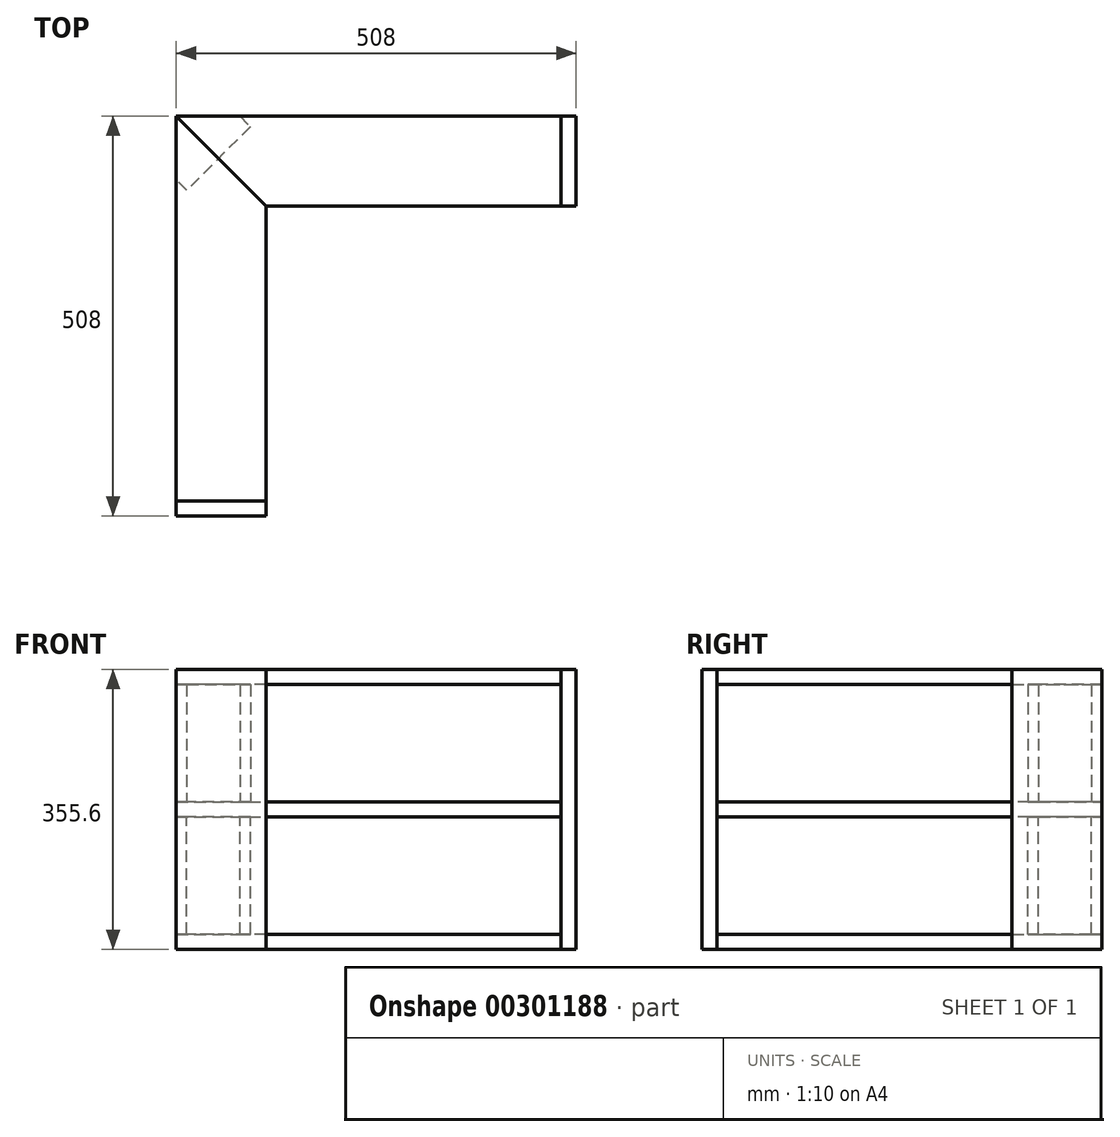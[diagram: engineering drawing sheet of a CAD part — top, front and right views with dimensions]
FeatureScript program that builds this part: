
annotation { "Feature Type Name" : "Feature", "Feature Type Description" : "" }
export const myFeature = defineFeature(function(context is Context, id is Id, definition is map)
    precondition{}
    {
        {
            var Q0;
            Q0=qCreatedBy(makeId("Top.planeOp"),FACE);
            var sketch = newSketch(context, id + "F0", { "sketchPlane" : qUnion([Q0])});
            skLineSegment(sketch, "E0", {"start": v(0, -374.65) * mm, "end": v(-114.3, -374.65) * mm});
            skLineSegment(sketch, "E1", {"start": v(-114.3, -374.65) * mm, "end": v(-114.3, 114.3) * mm});
            skLineSegment(sketch, "E2", {"start": v(-114.3, 114.3) * mm, "end": v(393.7, 114.3) * mm});
            skLineSegment(sketch, "E3", {"start": v(393.7, 114.3) * mm, "end": v(393.7, 0) * mm});
            skLineSegment(sketch, "E4", {"start": v(393.7, 0) * mm, "end": v(0, 0) * mm});
            skLineSegment(sketch, "E5", {"start": v(0, 0) * mm, "end": v(0, -374.65) * mm});
            skLineSegment(sketch, "E6", {"start": v(0, 0) * mm, "end": v(-114.3, 114.3) * mm});
            skSolve(sketch);
        }
        {
            var Q0;
            Q0=makeQuery(id+"F0.imprint","IMPRINT",FACE,{"disambiguationData":[TD([[makeQuery(id+"F0.imprint","IMPRINT",EDGE,{"derivedFrom":sQuery(id+"F0.wireOp",EDGE,"E0")}),-1.0]])]});
            extrude(context, id + "F1", {"entities" : qUnion([Q0]), "depth" : 19.05 * mm});
        }
        {
            var Q0;
            Q0=makeQuery(id+"F1.opExtrude","CAP_FACE",FACE,{"disambiguationData":[OSD([sQuery(id+"F0.wireOp",EDGE,"E0"),sQuery(id+"F0.wireOp",EDGE,"E1"),sQuery(id+"F0.wireOp",EDGE,"E5"),sQuery(id+"F0.wireOp",EDGE,"E6")])],"isStart":true});
            var sketch = newSketch(context, id + "F2", { "sketchPlane" : qUnion([Q0])});
            skLineSegment(sketch, "E7", {"start": v(-114.3, -114.3) * mm, "end": v(374.65, -114.3) * mm});
            skLineSegment(sketch, "E8", {"start": v(374.65, -114.3) * mm, "end": v(374.65, 0) * mm});
            skLineSegment(sketch, "E9", {"start": v(374.65, 0) * mm, "end": v(0, 0) * mm});
            skLineSegment(sketch, "E10", {"start": v(-114.3, -114.3) * mm, "end": v(0, 0) * mm});
            skSolve(sketch);
        }
        {
            var Q0;
            Q0=makeQuery(id+"F2.imprint","IMPRINT",FACE,{"disambiguationData":[TD([[makeQuery(id+"F2.imprint","IMPRINT",EDGE,{"derivedFrom":sQuery(id+"F2.wireOp",EDGE,"E7")}),1.0]])]});
            extrude(context, id + "F3", {"entities" : qUnion([Q0]), "oppositeDirection" : true, "depth" : 19.05 * mm});
        }
        {
            var Q0;
            Q0=makeQuery(id+"F1.opExtrude","SWEPT_FACE",FACE,{"disambiguationData":[OSD([sQuery(id+"F0.wireOp",EDGE,"E0")])]});
            var sketch = newSketch(context, id + "F4", { "sketchPlane" : qUnion([Q0])});
            skLineSegment(sketch, "E11.bottom", {"start": v(-114.3, 0) * mm, "end": v(0, 0) * mm});
            skLineSegment(sketch, "E11.top", {"start": v(-114.3, 355.6) * mm, "end": v(0, 355.6) * mm});
            skLineSegment(sketch, "E11.left", {"start": v(-114.3, 0) * mm, "end": v(-114.3, 355.6) * mm});
            skLineSegment(sketch, "E11.right", {"start": v(0, 0) * mm, "end": v(0, 355.6) * mm});
            skSolve(sketch);
        }
        {
            var Q0;
            {var subQ0=sQuery(id+"F4.wireOp",EDGE,"E11.top");Q0=makeQuery(id+"F4.imprint","IMPRINT",FACE,{"disambiguationData":[TD([[makeQuery(id+"F4.imprint","IMPRINT",EDGE,{"derivedFrom":subQ0}),-1.0]])]});}
            var Q1;
            {var subQ0=sQuery(id+"F4.wireOp",EDGE,"E11.bottom");Q1=makeQuery(id+"F4.imprint","IMPRINT",FACE,{"disambiguationData":[TD([[makeQuery(id+"F4.imprint","IMPRINT",EDGE,{"derivedFrom":subQ0}),-1.0]])]});}
            extrude(context, id + "F5", {"entities" : qUnion([Q0, Q1]), "depth" : 19.05 * mm});
        }
        {
            var Q0;
            Q0=makeQuery(id+"F3.opExtrude","SWEPT_FACE",FACE,{"disambiguationData":[OSD([sQuery(id+"F2.wireOp",EDGE,"E8")])]});
            var sketch = newSketch(context, id + "F6", { "sketchPlane" : qUnion([Q0])});
            skLineSegment(sketch, "E12.bottom", {"start": v(0, 0) * mm, "end": v(114.3, 0) * mm});
            skLineSegment(sketch, "E12.top", {"start": v(0, 355.6) * mm, "end": v(114.3, 355.6) * mm});
            skLineSegment(sketch, "E12.left", {"start": v(0, 0) * mm, "end": v(0, 355.6) * mm});
            skLineSegment(sketch, "E12.right", {"start": v(114.3, 0) * mm, "end": v(114.3, 355.6) * mm});
            skSolve(sketch);
        }
        {
            var Q0;
            {var subQ0=sQuery(id+"F6.wireOp",EDGE,"E12.top");Q0=makeQuery(id+"F6.imprint","IMPRINT",FACE,{"disambiguationData":[TD([[makeQuery(id+"F6.imprint","IMPRINT",EDGE,{"derivedFrom":subQ0}),-1.0]])]});}
            var Q1;
            {var subQ0=sQuery(id+"F6.wireOp",EDGE,"E12.bottom");Q1=makeQuery(id+"F6.imprint","IMPRINT",FACE,{"disambiguationData":[TD([[makeQuery(id+"F6.imprint","IMPRINT",EDGE,{"derivedFrom":subQ0}),-1.0]])]});}
            extrude(context, id + "F7", {"entities" : qUnion([Q0, Q1]), "depth" : 19.05 * mm});
        }
        {
            var Q0;
            Q0=makeQuery(id+"F1.opExtrude","CAP_FACE",FACE,{"disambiguationData":[OSD([sQuery(id+"F0.wireOp",EDGE,"E0"),sQuery(id+"F0.wireOp",EDGE,"E1"),sQuery(id+"F0.wireOp",EDGE,"E5"),sQuery(id+"F0.wireOp",EDGE,"E6")])],"isStart":true});
            cPlane(context, id + "F8", {"entities" : qUnion([Q0]), "cplaneType" : CPlaneType.OFFSET, "offset" : 355.6 * mm, "oppositeDirection" : true, "width" : 152.4 * mm, "height" : 152.4 * mm});
        }
        {
            var Q0;
            Q0=qCreatedBy(id+"F8.planeOp",FACE);
            var sketch = newSketch(context, id + "F9", { "sketchPlane" : qUnion([Q0])});
            skLineSegment(sketch, "E13", {"start": v(-114.3, -114.3) * mm, "end": v(-114.3, 374.65) * mm});
            skLineSegment(sketch, "E14", {"start": v(-114.3, 374.65) * mm, "end": v(0, 374.65) * mm});
            skLineSegment(sketch, "E15", {"start": v(0, 374.65) * mm, "end": v(0, 0) * mm});
            skLineSegment(sketch, "E16", {"start": v(0, 0) * mm, "end": v(-114.3, -114.3) * mm});
            skSolve(sketch);
        }
        {
            var Q0;
            Q0 = qSketchRegion(id + "F9", true);
            extrude(context, id + "F10", {"entities" : qUnion([Q0]), "depth" : 19.05 * mm});
        }
        {
            var Q0;
            Q0=qCreatedBy(id+"F8.planeOp",FACE);
            var sketch = newSketch(context, id + "F11", { "sketchPlane" : qUnion([Q0])});
            skLineSegment(sketch, "E17", {"start": v(0, 0) * mm, "end": v(-114.3, -114.3) * mm});
            skLineSegment(sketch, "E18", {"start": v(-114.3, -114.3) * mm, "end": v(374.65, -114.3) * mm});
            skLineSegment(sketch, "E19", {"start": v(374.65, -114.3) * mm, "end": v(374.65, 0) * mm});
            skLineSegment(sketch, "E20", {"start": v(374.65, 0) * mm, "end": v(0, 0) * mm});
            skSolve(sketch);
        }
        {
            var Q0;
            Q0=makeQuery(id+"F11.imprint","IMPRINT",FACE,{"disambiguationData":[TD([[makeQuery(id+"F11.imprint","IMPRINT",EDGE,{"derivedFrom":sQuery(id+"F11.wireOp",EDGE,"E17")}),1.0]])]});
            extrude(context, id + "F12", {"entities" : qUnion([Q0]), "depth" : 19.05 * mm});
        }
        {
            var Q0;
            Q0=makeQuery(id+"F10.opExtrude","CAP_FACE",FACE,{"disambiguationData":[OSD([sQuery(id+"F9.wireOp",EDGE,"E13"),sQuery(id+"F9.wireOp",EDGE,"E14"),sQuery(id+"F9.wireOp",EDGE,"E15"),sQuery(id+"F9.wireOp",EDGE,"E16")])],"isStart":false});
            var Q1;
            Q1=makeQuery(id+"F1.opExtrude","CAP_FACE",FACE,{"disambiguationData":[OSD([sQuery(id+"F0.wireOp",EDGE,"E0"),sQuery(id+"F0.wireOp",EDGE,"E1"),sQuery(id+"F0.wireOp",EDGE,"E5"),sQuery(id+"F0.wireOp",EDGE,"E6")])],"isStart":false});
            cPlane(context, id + "F13", {"entities" : qUnion([Q0, Q1]), "cplaneType" : CPlaneType.MID_PLANE, "offset" : 25.4 * mm, "width" : 152.4 * mm, "height" : 152.4 * mm});
        }
        {
            var Q0;
            Q0=qCreatedBy(id+"F13.planeOp",FACE);
            var sketch = newSketch(context, id + "F14", { "sketchPlane" : qUnion([Q0])});
            skLineSegment(sketch, "E21", {"start": v(-114.3, 374.65) * mm, "end": v(0, 374.65) * mm});
            skLineSegment(sketch, "E22", {"start": v(0, 374.65) * mm, "end": v(0, 0) * mm});
            skLineSegment(sketch, "E23", {"start": v(0, 0) * mm, "end": v(-114.3, -114.3) * mm});
            skLineSegment(sketch, "E24", {"start": v(-114.3, -114.3) * mm, "end": v(-114.3, 374.65) * mm});
            skSolve(sketch);
        }
        {
            var Q0;
            Q0=makeQuery(id+"F14.imprint","IMPRINT",FACE,{"disambiguationData":[TD([[makeQuery(id+"F14.imprint","IMPRINT",EDGE,{"derivedFrom":sQuery(id+"F14.wireOp",EDGE,"E21")}),-1.0]])]});
            extrude(context, id + "F15", {"entities" : qUnion([Q0]), "endBound" : BoundingType.SYMMETRIC, "depth" : 19.05 * mm});
        }
        {
            var Q0;
            Q0=qCreatedBy(id+"F13.planeOp",FACE);
            var sketch = newSketch(context, id + "F16", { "sketchPlane" : qUnion([Q0])});
            skLineSegment(sketch, "E25", {"start": v(-114.3, -114.3) * mm, "end": v(0, 0) * mm});
            skLineSegment(sketch, "E26", {"start": v(0, 0) * mm, "end": v(374.65, 0) * mm});
            skLineSegment(sketch, "E27", {"start": v(374.65, 0) * mm, "end": v(374.65, -114.3) * mm});
            skLineSegment(sketch, "E28", {"start": v(374.65, -114.3) * mm, "end": v(-114.3, -114.3) * mm});
            skSolve(sketch);
        }
        {
            var Q0;
            Q0=makeQuery(id+"F16.imprint","IMPRINT",FACE,{"disambiguationData":[TD([[makeQuery(id+"F16.imprint","IMPRINT",EDGE,{"derivedFrom":sQuery(id+"F16.wireOp",EDGE,"E25")}),-1.0]])]});
            extrude(context, id + "F17", {"entities" : qUnion([Q0]), "endBound" : BoundingType.SYMMETRIC, "depth" : 19.05 * mm});
        }
        {
            var Q0;
            Q0=makeQuery(id+"F17.opExtrude","CAP_FACE",FACE,{"disambiguationData":[OSD([sQuery(id+"F16.wireOp",EDGE,"E25"),sQuery(id+"F16.wireOp",EDGE,"E26"),sQuery(id+"F16.wireOp",EDGE,"E27"),sQuery(id+"F16.wireOp",EDGE,"E28")])],"isStart":true});
            var sketch = newSketch(context, id + "F18", { "sketchPlane" : qUnion([Q0])});
            skLineSegment(sketch, "E29", {"start": v(-33.48, 114.3) * mm, "end": v(-20, 100.83) * mm});
            skLineSegment(sketch, "E30", {"start": v(-20, 100.83) * mm, "end": v(-100.83, 20) * mm});
            skLineSegment(sketch, "E31", {"start": v(-100.83, 20) * mm, "end": v(-114.3, 33.48) * mm});
            skLineSegment(sketch, "E32", {"start": v(-114.3, 33.48) * mm, "end": v(-33.48, 114.3) * mm});
            skSolve(sketch);
        }
        {
            var Q0;
            {var subQ0=sQuery(id+"F18.wireOp",EDGE,"E29");Q0=makeQuery(id+"F18.imprint","IMPRINT",FACE,{"disambiguationData":[TD([[makeQuery(id+"F18.imprint","IMPRINT",EDGE,{"derivedFrom":subQ0}),-1.0]])]});}
            var Q1;
            {var subQ0=sQuery(id+"F18.wireOp",EDGE,"E31");Q1=makeQuery(id+"F18.imprint","IMPRINT",FACE,{"disambiguationData":[TD([[makeQuery(id+"F18.imprint","IMPRINT",EDGE,{"derivedFrom":subQ0}),-1.0]])]});}
            var Q2;
            Q2=makeQuery(id+"F12.opExtrude","CAP_FACE",FACE,{"disambiguationData":[OSD([sQuery(id+"F11.wireOp",EDGE,"E17"),sQuery(id+"F11.wireOp",EDGE,"E18"),sQuery(id+"F11.wireOp",EDGE,"E19"),sQuery(id+"F11.wireOp",EDGE,"E20")])],"isStart":false});
            extrude(context, id + "F19", {"entities" : qUnion([Q0, Q1]), "endBound" : BoundingType.UP_TO_SURFACE, "endBoundEntityFace" : qUnion([Q2]), "depth" : 25.4 * mm});
        }
        {
            var Q0;
            Q0=makeQuery(id+"F17.opExtrude","CAP_FACE",FACE,{"disambiguationData":[OSD([sQuery(id+"F16.wireOp",EDGE,"E25"),sQuery(id+"F16.wireOp",EDGE,"E26"),sQuery(id+"F16.wireOp",EDGE,"E27"),sQuery(id+"F16.wireOp",EDGE,"E28")])],"isStart":false});
            var sketch = newSketch(context, id + "F20", { "sketchPlane" : qUnion([Q0])});
            skLineSegment(sketch, "E33", {"start": v(-33.48, -114.3) * mm, "end": v(-20, -100.83) * mm});
            skLineSegment(sketch, "E34", {"start": v(-20, -100.83) * mm, "end": v(-100.83, -20) * mm});
            skLineSegment(sketch, "E35", {"start": v(-100.83, -20) * mm, "end": v(-114.3, -33.48) * mm});
            skLineSegment(sketch, "E36", {"start": v(-114.3, -33.48) * mm, "end": v(-33.48, -114.3) * mm});
            skSolve(sketch);
        }
        {
            var Q0;
            {var subQ0=sQuery(id+"F20.wireOp",EDGE,"E35");Q0=makeQuery(id+"F20.imprint","IMPRINT",FACE,{"disambiguationData":[TD([[makeQuery(id+"F20.imprint","IMPRINT",EDGE,{"derivedFrom":subQ0}),1.0]])]});}
            var Q1;
            {var subQ0=sQuery(id+"F20.wireOp",EDGE,"E33");Q1=makeQuery(id+"F20.imprint","IMPRINT",FACE,{"disambiguationData":[TD([[makeQuery(id+"F20.imprint","IMPRINT",EDGE,{"derivedFrom":subQ0}),1.0]])]});}
            var Q2;
            Q2=makeQuery(id+"F3.opExtrude","CAP_FACE",FACE,{"disambiguationData":[OSD([sQuery(id+"F2.wireOp",EDGE,"E7"),sQuery(id+"F2.wireOp",EDGE,"E8"),sQuery(id+"F2.wireOp",EDGE,"E9"),sQuery(id+"F2.wireOp",EDGE,"E10")])],"isStart":false});
            extrude(context, id + "F21", {"entities" : qUnion([Q0, Q1]), "endBound" : BoundingType.UP_TO_SURFACE, "endBoundEntityFace" : qUnion([Q2]), "depth" : 25.4 * mm});
        }
    });
